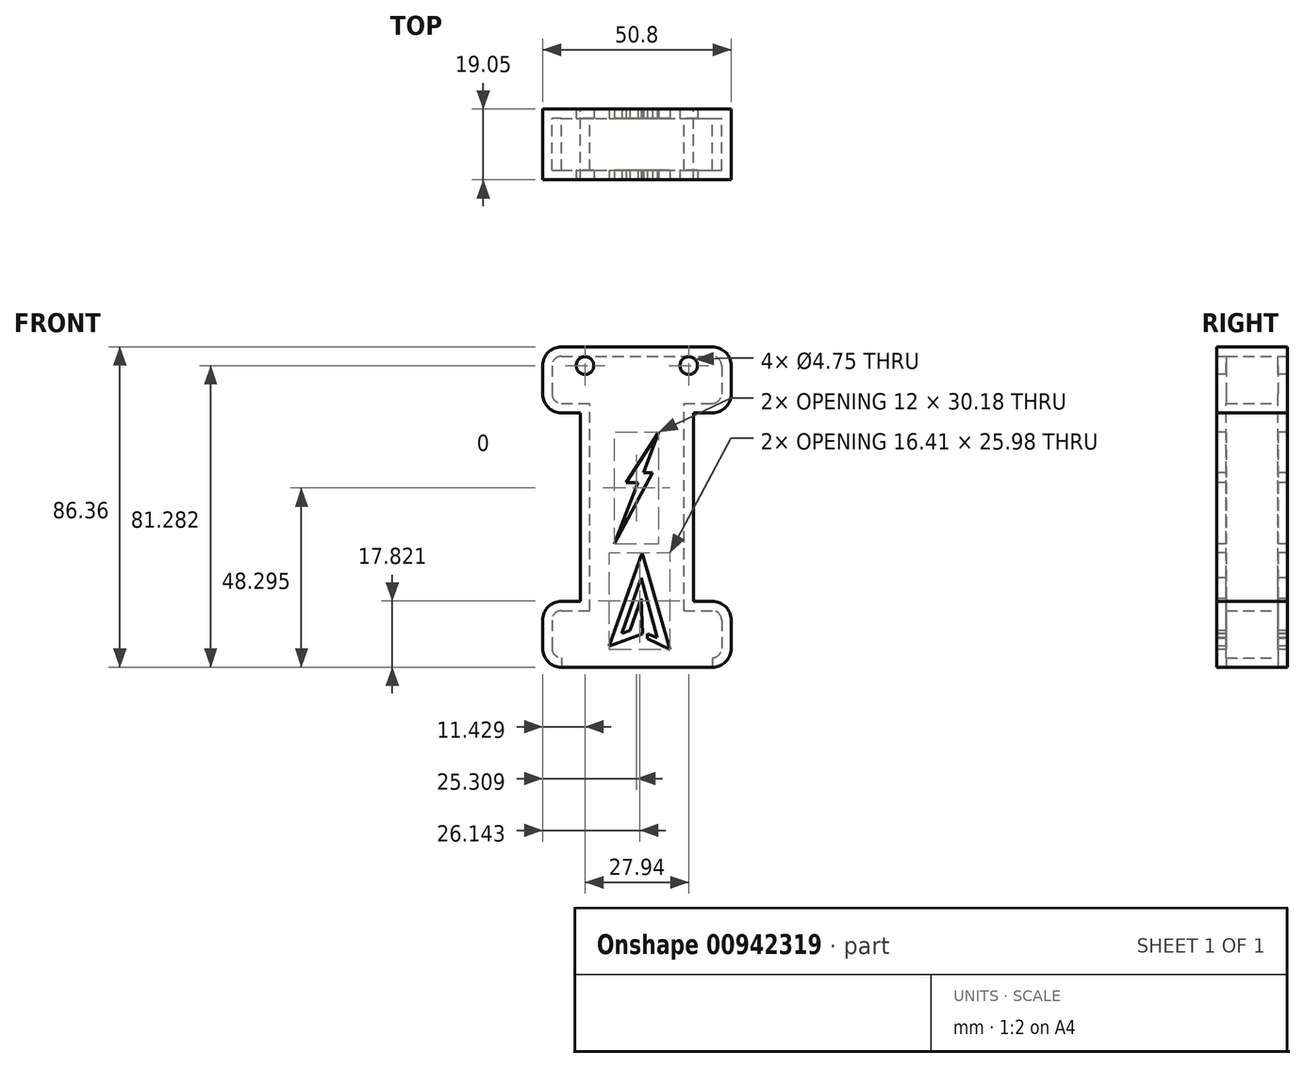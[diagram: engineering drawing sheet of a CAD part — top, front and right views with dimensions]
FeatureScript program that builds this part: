
annotation { "Feature Type Name" : "Feature", "Feature Type Description" : "" }
export const myFeature = defineFeature(function(context is Context, id is Id, definition is map)
    precondition{}
    {
        {
            var Q0;
            Q0=qCreatedBy(makeId("Front.planeOp"),FACE);
            var sketch = newSketch(context, id + "F0", { "sketchPlane" : qUnion([Q0])});
            skLineSegment(sketch, "E0.bottom", {"start": v(-34.35, 29.33) * mm, "end": v(16.45, 29.33) * mm});
            skLineSegment(sketch, "E0.top", {"start": v(-34.35, 11.55) * mm, "end": v(16.45, 11.55) * mm});
            skLineSegment(sketch, "E0.left", {"start": v(-34.35, 29.33) * mm, "end": v(-34.35, 11.55) * mm});
            skLineSegment(sketch, "E0.right", {"start": v(16.45, 29.33) * mm, "end": v(16.45, 11.55) * mm});
            skLineSegment(sketch, "E1.bottom", {"start": v(-34.35, -39.25) * mm, "end": v(16.45, -39.25) * mm});
            skLineSegment(sketch, "E1.top", {"start": v(-34.35, -57.03) * mm, "end": v(16.45, -57.03) * mm});
            skLineSegment(sketch, "E1.left", {"start": v(-34.35, -39.25) * mm, "end": v(-34.35, -57.03) * mm});
            skLineSegment(sketch, "E1.right", {"start": v(16.45, -39.25) * mm, "end": v(16.45, -57.03) * mm});
            skLineSegment(sketch, "E2.bottom", {"start": v(-24.2, -39.25) * mm, "end": v(6.29, -39.25) * mm});
            skLineSegment(sketch, "E2.top", {"start": v(-24.2, 11.55) * mm, "end": v(6.29, 11.55) * mm});
            skLineSegment(sketch, "E2.left", {"start": v(-24.2, -39.25) * mm, "end": v(-24.2, 11.55) * mm});
            skLineSegment(sketch, "E2.right", {"start": v(6.29, -39.25) * mm, "end": v(6.29, 11.55) * mm});
            skSolve(sketch);
        }
        {
            var Q0;
            {var subQ0=sQuery(id+"F0.wireOp",EDGE,"E2.left");Q0=makeQuery(id+"F0.imprint","IMPRINT",FACE,{"disambiguationData":[TD([[makeQuery(id+"F0.imprint","IMPRINT",EDGE,{"derivedFrom":subQ0}),-1.0]])]});}
            var Q1;
            Q1=makeQuery(id+"F0.imprint","IMPRINT",FACE,{"disambiguationData":[TD([[makeQuery(id+"F0.imprint","IMPRINT",EDGE,{"derivedFrom":sQuery(id+"F0.wireOp",EDGE,"E1.top")}),1.0]])]});
            var Q2;
            Q2=makeQuery(id+"F0.imprint","IMPRINT",FACE,{"disambiguationData":[TD([[makeQuery(id+"F0.imprint","IMPRINT",EDGE,{"derivedFrom":sQuery(id+"F0.wireOp",EDGE,"E0.bottom")}),-1.0]])]});
            extrude(context, id + "F1", {"entities" : qUnion([Q0, Q1, Q2]), "depth" : 19.05 * mm});
        }
        {
            var Q0;
            Q0=makeQuery(id+"F1.opExtrude","SWEPT_EDGE",EDGE,{"disambiguationData":[OSD([sQuery(id+"F0.wireOp",EDGE,"E0.top"),sQuery(id+"F0.wireOp",EDGE,"E0.left")])]});
            var Q1;
            Q1=makeQuery(id+"F1.opExtrude","SWEPT_EDGE",EDGE,{"disambiguationData":[OSD([sQuery(id+"F0.wireOp",EDGE,"E0.top"),sQuery(id+"F0.wireOp",EDGE,"E0.right")])]});
            var Q2;
            Q2=makeQuery(id+"F1.opExtrude","SWEPT_EDGE",EDGE,{"disambiguationData":[OSD([sQuery(id+"F0.wireOp",EDGE,"E0.bottom"),sQuery(id+"F0.wireOp",EDGE,"E0.right")])]});
            var Q3;
            Q3=makeQuery(id+"F1.opExtrude","SWEPT_EDGE",EDGE,{"disambiguationData":[OSD([sQuery(id+"F0.wireOp",EDGE,"E0.bottom"),sQuery(id+"F0.wireOp",EDGE,"E0.left")])]});
            var Q4;
            Q4=makeQuery(id+"F1.opExtrude","SWEPT_EDGE",EDGE,{"disambiguationData":[OSD([sQuery(id+"F0.wireOp",EDGE,"E1.bottom"),sQuery(id+"F0.wireOp",EDGE,"E1.left")])]});
            var Q5;
            Q5=makeQuery(id+"F1.opExtrude","SWEPT_EDGE",EDGE,{"disambiguationData":[OSD([sQuery(id+"F0.wireOp",EDGE,"E1.top"),sQuery(id+"F0.wireOp",EDGE,"E1.left")])]});
            var Q6;
            Q6=makeQuery(id+"F1.opExtrude","SWEPT_EDGE",EDGE,{"disambiguationData":[OSD([sQuery(id+"F0.wireOp",EDGE,"E1.top"),sQuery(id+"F0.wireOp",EDGE,"E1.right")])]});
            var Q7;
            Q7=makeQuery(id+"F1.opExtrude","SWEPT_EDGE",EDGE,{"disambiguationData":[OSD([sQuery(id+"F0.wireOp",EDGE,"E1.bottom"),sQuery(id+"F0.wireOp",EDGE,"E1.right")])]});
            fillet(context, id + "F2", {"entities" : qUnion([Q0, Q1, Q2, Q3, Q4, Q5, Q6, Q7]), "radius" : 5.08 * mm, "tangentPropagation" : true, "allowEdgeOverflow" : false});
        }
        {
            var Q0;
            Q0=makeQuery(id+"F1.opExtrude","CAP_FACE",FACE,{"disambiguationData":[OSD([sQuery(id+"F0.wireOp",EDGE,"E0.bottom"),sQuery(id+"F0.wireOp",EDGE,"E0.top"),sQuery(id+"F0.wireOp",EDGE,"E0.left"),sQuery(id+"F0.wireOp",EDGE,"E0.right"),sQuery(id+"F0.wireOp",EDGE,"E1.bottom"),sQuery(id+"F0.wireOp",EDGE,"E1.top"),sQuery(id+"F0.wireOp",EDGE,"E1.left"),sQuery(id+"F0.wireOp",EDGE,"E1.right"),sQuery(id+"F0.wireOp",EDGE,"E2.left"),sQuery(id+"F0.wireOp",EDGE,"E2.right")])],"isStart":false});
            var sketch = newSketch(context, id + "F3", { "sketchPlane" : qUnion([Q0])});
            skCircle(sketch, "E3", {"center": v(-22.92, 24.25) * mm, "radius": 2.37 * mm});
            skCircle(sketch, "E4.MirrorC", {"center": v(5.02, 24.25) * mm, "radius": 2.37 * mm});
            skSolve(sketch);
        }
        {
            var Q0;
            Q0=makeQuery(id+"F1.opExtrude","SWEPT_FACE",FACE,{"disambiguationData":[OSD([sQuery(id+"F0.wireOp",EDGE,"E1.top")])]});
            shell(context, id + "F4", {"entities" : qUnion([Q0]), "thickness" : 2.54 * mm});
        }
        {
            var Q0;
            Q0=qSketchRegion(id+"F3",true);
            extrude(context, id + "F5", {"entities" : qUnion([Q0]), "operationType" : NewBodyOperationType.REMOVE, "oppositeDirection" : true, "depth" : 45.6 * mm});
        }
        {
            var Q0;
            Q0=makeQuery(id+"F1.opExtrude","CAP_FACE",FACE,{"disambiguationData":[OSD([sQuery(id+"F0.wireOp",EDGE,"E0.bottom"),sQuery(id+"F0.wireOp",EDGE,"E0.top"),sQuery(id+"F0.wireOp",EDGE,"E0.left"),sQuery(id+"F0.wireOp",EDGE,"E0.right"),sQuery(id+"F0.wireOp",EDGE,"E1.bottom"),sQuery(id+"F0.wireOp",EDGE,"E1.top"),sQuery(id+"F0.wireOp",EDGE,"E1.left"),sQuery(id+"F0.wireOp",EDGE,"E1.right"),sQuery(id+"F0.wireOp",EDGE,"E2.left"),sQuery(id+"F0.wireOp",EDGE,"E2.right")])],"isStart":false});
            var sketch = newSketch(context, id + "F6", { "sketchPlane" : qUnion([Q0])});
            skLineSegment(sketch, "E5", {"start": v(-3.04, 6.35) * mm, "end": v(-11.84, -7.3) * mm});
            skLineSegment(sketch, "E6", {"start": v(-11.84, -7.3) * mm, "end": v(-8.68, -7.3) * mm});
            skLineSegment(sketch, "E7", {"start": v(-8.68, -7.3) * mm, "end": v(-15.04, -23.82) * mm});
            skLineSegment(sketch, "E8", {"start": v(-15.04, -23.82) * mm, "end": v(-4.7, -4.55) * mm});
            skLineSegment(sketch, "E9", {"start": v(-4.7, -4.55) * mm, "end": v(-7.22, -4.55) * mm});
            skLineSegment(sketch, "E10", {"start": v(-7.22, -4.55) * mm, "end": v(-3.04, 6.35) * mm});
            skLineSegment(sketch, "E11", {"start": v(-16.41, -51.38) * mm, "end": v(-7.56, -26.22) * mm});
            skLineSegment(sketch, "E12", {"start": v(-7.56, -26.22) * mm, "end": v(0, -52.2) * mm});
            skLineSegment(sketch, "E13", {"start": v(0, -52.2) * mm, "end": v(-6.12, -49.26) * mm});
            skLineSegment(sketch, "E14", {"start": v(-6.12, -49.26) * mm, "end": v(-6.12, -48.07) * mm});
            skLineSegment(sketch, "E15", {"start": v(-6.12, -48.07) * mm, "end": v(-3.47, -49) * mm});
            skLineSegment(sketch, "E16", {"start": v(-3.47, -49) * mm, "end": v(-7.8, -32.93) * mm});
            skLineSegment(sketch, "E17", {"start": v(-16.41, -51.38) * mm, "end": v(-7.44, -48.07) * mm});
            skLineSegment(sketch, "E18", {"start": v(-7.44, -48.07) * mm, "end": v(-7.8, -38.58) * mm});
            skLineSegment(sketch, "E19", {"start": v(-7.8, -38.58) * mm, "end": v(-10.8, -47.17) * mm});
            skLineSegment(sketch, "E20", {"start": v(-10.8, -47.17) * mm, "end": v(-13.02, -47.86) * mm});
            skLineSegment(sketch, "E21", {"start": v(-13.02, -47.86) * mm, "end": v(-7.8, -32.93) * mm});
            skSolve(sketch);
        }
        {
            var Q0;
            Q0=makeQuery(id+"F6.imprint","IMPRINT",FACE,{"disambiguationData":[TD([[makeQuery(id+"F6.imprint","IMPRINT",EDGE,{"derivedFrom":sQuery(id+"F6.wireOp",EDGE,"E5")}),1.0]])]});
            extrude(context, id + "F7", {"entities" : qUnion([Q0]), "operationType" : NewBodyOperationType.REMOVE, "oppositeDirection" : true, "depth" : 16.68 * mm});
        }
        {
            var Q0;
            Q0=qSketchRegion(id+"F6",true);
            extrude(context, id + "F8", {"entities" : qUnion([Q0]), "operationType" : NewBodyOperationType.REMOVE, "oppositeDirection" : true, "depth" : 25.4 * mm});
        }
    });
